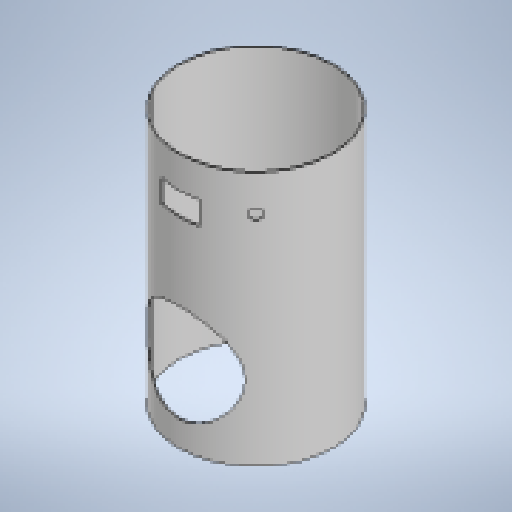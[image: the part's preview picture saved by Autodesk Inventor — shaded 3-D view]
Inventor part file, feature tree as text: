
AUTODESK INVENTOR PART (.ipt)
format: ipt  version: 2025.3 (Build 293356030, 356C)  size: 332,800 bytes
history: native  units: mm
features: sketch x7, other x7, extrude x3, plane x2, revolve x1
ambient origin geometry x8: Origin, YZ Plane, XZ Plane, XY Plane, X Axis, Y Axis, Z Axis, Center Point
bodies: Body1 (feature_tree)
feature tree (20):
  sketch  "Sketch13"  dims[d53=850.0mm d54=10.12291mm]
  other  "WeldJoint"
  other  "Outer"
  other  "Clock_Feeder"
  other  "Charging"
  other  "Accsess"
  revolve  "Revolution2"  [1 undecoded]
  sketch  "Sketch AnglePlane_Feeder"  dims[d63=850.0mm d64=90.0deg d66=59.0mm d67=0.0mm d68=0.0mm d69=537.0mm d71=140.0mm d72=0.0mm d73=0.0mm d74=1100.0mm d76=850.0mm d77=90.0deg d78=207.0mm d79=125.0mm d80=0.0mm d81=0.0mm d3=0.872665mm d4=0.872665mm]
  other  "AnglePlane_Feeder"
  extrude  "Extrusion7"  TaperAngle=0.0deg  [1 undecoded]
  plane  "Work Plane16"
  extrude  "Extrusion8"  Depth=10.995574mm
  sketch  "Sketch19"  dims[d61=850.0mm]
  plane  "Work Plane18"
  extrude  "Extrusion9"  Depth=1400.0mm
  sketch  "Sketch14"  dims[d55=0.0mm d56=0.0mm]
  sketch  "Sketch16"  dims[d57=315.0deg d58=10.995574mm]
  sketch  "Sketch17"  dims[d59=1400.0mm d60=6.0mm]
  sketch  "Sketch20"  dims[d62=62.8144mm]
  other  "Definition1"
note: 2 required parameter values undecoded (feature->parameter linkage not recoverable at this tier; creation-order binding heuristic only, values carry confidence <= 0.55)